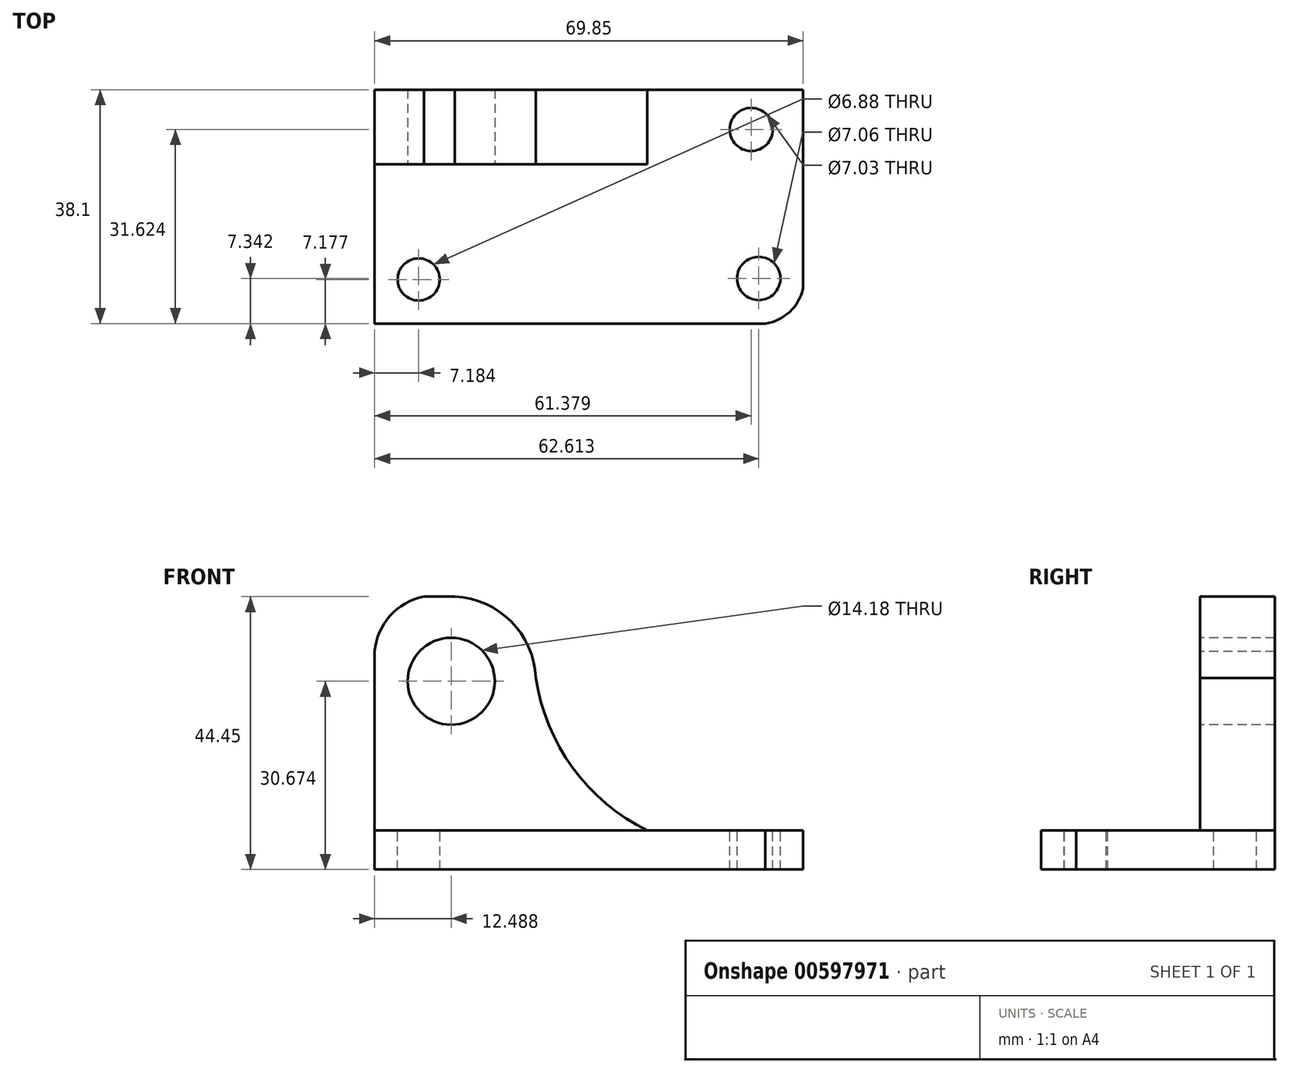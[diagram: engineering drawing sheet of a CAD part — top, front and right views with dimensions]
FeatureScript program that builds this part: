
annotation { "Feature Type Name" : "Feature", "Feature Type Description" : "" }
export const myFeature = defineFeature(function(context is Context, id is Id, definition is map)
    precondition{}
    {
        {
            var Q0;
            Q0=qCreatedBy(makeId("Front.planeOp"),FACE);
            var sketch = newSketch(context, id + "F0", { "sketchPlane" : qUnion([Q0])});
            skLineSegment(sketch, "E0", {"start": v(-44.83, 44.45) * mm, "end": v(-44.83, 0) * mm});
            skLineSegment(sketch, "E1", {"start": v(-44.83, 0) * mm, "end": v(25.02, 0) * mm});
            skLineSegment(sketch, "E2", {"start": v(25.02, 0) * mm, "end": v(25.02, 44.45) * mm});
            skLineSegment(sketch, "E3", {"start": v(25.02, 44.45) * mm, "end": v(-44.83, 44.45) * mm});
            skSolve(sketch);
        }
        {
            var Q0;
            Q0=makeQuery(id+"F0.imprint","IMPRINT",FACE,{"disambiguationData":[TD([[makeQuery(id+"F0.imprint","IMPRINT",EDGE,{"derivedFrom":sQuery(id+"F0.wireOp",EDGE,"E0")}),1.0]])]});
            extrude(context, id + "F1", {"entities" : qUnion([Q0]), "depth" : 38.1 * mm, "offsetDistance" : 25.4 * mm});
        }
        {
            var Q0;
            Q0=makeQuery(id+"F1.opExtrude","SWEPT_FACE",FACE,{"disambiguationData":[OSD([sQuery(id+"F0.wireOp",EDGE,"E3")])]});
            var sketch = newSketch(context, id + "F2", { "sketchPlane" : qUnion([Q0])});
            skArc(sketch, "E4", {"start": v(-44.83, -31.23) * mm, "mid": v(-42.48, -36.24) * mm, "end": v(-37.27, -38.1) * mm});
            skArc(sketch, "E5", {"start": v(18.85, -38.1) * mm, "mid": v(22.83, -36.2) * mm, "end": v(25.02, -32.38) * mm});
            skSolve(sketch);
        }
        {
            var Q0;
            {var subQ0=sQuery(id+"F2.wireOp",EDGE,"E4");var subQ1=sQuery(id+"F0.wireOp",EDGE,"E3");var subQ4=makeQuery(id+"F1.opExtrude","CAP_EDGE",EDGE,{"disambiguationData":[OSD([subQ1])],"isStart":false});var subQ5=makeQuery(id+"F2.imprint","INTERSECT",VERTEX,{"disambiguationData":[OD(1.0)],"derivedFrom":[subQ4,subQ0]});Q0=makeQuery(id+"F2.imprint","IMPRINT",FACE,{"disambiguationData":[TD([[makeQuery(id+"F2.imprint","IMPRINT",EDGE,{"disambiguationData":[TD([[subQ5,1.0]])],"derivedFrom":subQ0}),-1.0]])]});}
            var Q1;
            {var subQ0=sQuery(id+"F2.wireOp",EDGE,"E5");Q1=makeQuery(id+"F2.imprint","IMPRINT",FACE,{"disambiguationData":[TD([[makeQuery(id+"F2.imprint","IMPRINT",EDGE,{"derivedFrom":subQ0}),-1.0]])]});}
            extrude(context, id + "F3", {"entities" : qUnion([Q0, Q1]), "operationType" : NewBodyOperationType.REMOVE, "endBound" : BoundingType.THROUGH_ALL, "oppositeDirection" : true, "depth" : 25.4 * mm, "offsetDistance" : 25.4 * mm});
        }
        {
            var Q0;
            Q0=makeQuery(id+"F1.opExtrude","SWEPT_FACE",FACE,{"disambiguationData":[OSD([sQuery(id+"F0.wireOp",EDGE,"E3")])]});
            var sketch = newSketch(context, id + "F4", { "sketchPlane" : qUnion([Q0])});
            skLineSegment(sketch, "E6", {"start": v(-44.83, -12.18) * mm, "end": v(-0.38, -12.18) * mm});
            skLineSegment(sketch, "E7", {"start": v(-0.38, -12.18) * mm, "end": v(-0.38, 0) * mm});
            skSolve(sketch);
        }
        {
            var Q0;
            {var subQ2=sQuery(id+"F4.wireOp",EDGE,"E6");Q0=makeQuery(id+"F4.imprint","IMPRINT",FACE,{"disambiguationData":[TD([[makeQuery(id+"F4.imprint","IMPRINT",EDGE,{"derivedFrom":subQ2}),-1.0]])]});}
            extrude(context, id + "F5", {"entities" : qUnion([Q0]), "operationType" : NewBodyOperationType.REMOVE, "oppositeDirection" : true, "depth" : 31.75 * mm, "offsetDistance" : 25.4 * mm});
        }
        {
            var Q0;
            Q0=makeQuery(id+"F5.boolean.opBoolean","COPY",FACE,{"derivedFrom":makeQuery(id+"F5.opExtrude","CAP_FACE",FACE,{"disambiguationData":[OSD([sQuery(id+"F0.wireOp",EDGE,"E0"),sQuery(id+"F0.wireOp",EDGE,"E2"),sQuery(id+"F0.wireOp",EDGE,"E3"),sQuery(id+"F2.wireOp",EDGE,"E4"),sQuery(id+"F2.wireOp",EDGE,"E5"),sQuery(id+"F4.wireOp",EDGE,"E6"),sQuery(id+"F4.wireOp",EDGE,"E7")])],"isStart":false})});
            extrude(context, id + "F6", {"entities" : qUnion([Q0]), "operationType" : NewBodyOperationType.ADD, "depth" : 5.08 * mm, "offsetDistance" : 25.4 * mm});
        }
        {
            var Q0;
            Q0=makeQuery(id+"F6.opExtrude","CAP_FACE",FACE,{"disambiguationData":[OSD([sQuery(id+"F0.wireOp",EDGE,"E0"),sQuery(id+"F0.wireOp",EDGE,"E2"),sQuery(id+"F0.wireOp",EDGE,"E3"),sQuery(id+"F2.wireOp",EDGE,"E4"),sQuery(id+"F2.wireOp",EDGE,"E5"),sQuery(id+"F4.wireOp",EDGE,"E6"),sQuery(id+"F4.wireOp",EDGE,"E7")])],"isStart":false});
            extrude(context, id + "F7", {"entities" : qUnion([Q0]), "operationType" : NewBodyOperationType.REMOVE, "oppositeDirection" : true, "depth" : 6.35 * mm, "offsetDistance" : 25.4 * mm});
        }
        {
            var Q0;
            Q0=makeQuery(id+"F7.boolean.opBoolean","COPY",FACE,{"derivedFrom":makeQuery(id+"F7.opExtrude","CAP_FACE",FACE,{"disambiguationData":[OSD([sQuery(id+"F0.wireOp",EDGE,"E0"),sQuery(id+"F0.wireOp",EDGE,"E2"),sQuery(id+"F0.wireOp",EDGE,"E3"),sQuery(id+"F2.wireOp",EDGE,"E4"),sQuery(id+"F2.wireOp",EDGE,"E5"),sQuery(id+"F4.wireOp",EDGE,"E6"),sQuery(id+"F4.wireOp",EDGE,"E7")])],"isStart":false})});
            extrude(context, id + "F8", {"entities" : qUnion([Q0]), "operationType" : NewBodyOperationType.REMOVE, "oppositeDirection" : true, "depth" : 5.08 * mm, "offsetDistance" : 25.4 * mm});
        }
        {
            var Q0;
            {var subQ0=sQuery(id+"F4.wireOp",EDGE,"E6");Q0=makeQuery(id+"F8.boolean.opBoolean","MERGE",FACE,{"derivedFrom":[makeQuery(id+"F7.boolean.opBoolean","MERGE",FACE,{"derivedFrom":[makeQuery(id+"F5.boolean.opBoolean","COPY",FACE,{"derivedFrom":makeQuery(id+"F5.opExtrude","SWEPT_FACE",FACE,{"disambiguationData":[OSD([subQ0])]})}),makeQuery(id+"F7.opExtrude","SWEPT_FACE",FACE,{"disambiguationData":[OSD([subQ0])]})]}),makeQuery(id+"F8.opExtrude","SWEPT_FACE",FACE,{"disambiguationData":[OSD([subQ0])]})]});}
            var sketch = newSketch(context, id + "F9", { "sketchPlane" : qUnion([Q0])});
            skArc(sketch, "E8", {"start": v(-32.95, 44.45) * mm, "mid": v(-40.87, 42.63) * mm, "end": v(-44.83, 35.54) * mm});
            skArc(sketch, "E9", {"start": v(-18.56, 31.23) * mm, "mid": v(-23.01, 40.83) * mm, "end": v(-32.95, 44.45) * mm});
            skArc(sketch, "E10", {"start": v(-18.56, 31.23) * mm, "mid": v(-12.52, 16.56) * mm, "end": v(-0.38, 6.35) * mm});
            skSolve(sketch);
        }
        {
            var Q0;
            {var subQ0=sQuery(id+"F9.wireOp",EDGE,"E8");var subQ1=sQuery(id+"F4.wireOp",EDGE,"E6");var subQ6=makeQuery(id+"F5.boolean.opBoolean","COPY",EDGE,{"derivedFrom":makeQuery(id+"F5.opExtrude","CAP_EDGE",EDGE,{"disambiguationData":[OSD([subQ1])],"isStart":true})});var subQ7=makeQuery(id+"F9.imprint","INTERSECT",VERTEX,{"derivedFrom":[subQ6,subQ0]});Q0=makeQuery(id+"F9.imprint","IMPRINT",FACE,{"disambiguationData":[TD([[makeQuery(id+"F9.imprint","IMPRINT",EDGE,{"disambiguationData":[TD([[subQ7,-1.0]])],"derivedFrom":subQ0}),-1.0]])]});}
            var Q1;
            {var subQ0=sQuery(id+"F9.wireOp",EDGE,"E10");Q1=makeQuery(id+"F9.imprint","IMPRINT",FACE,{"disambiguationData":[TD([[makeQuery(id+"F9.imprint","IMPRINT",EDGE,{"derivedFrom":subQ0}),1.0]])]});}
            extrude(context, id + "F10", {"entities" : qUnion([Q0, Q1]), "operationType" : NewBodyOperationType.REMOVE, "endBound" : BoundingType.THROUGH_ALL, "oppositeDirection" : true, "depth" : 25.4 * mm, "offsetDistance" : 25.4 * mm});
        }
        {
            var Q0;
            {var subQ0=sQuery(id+"F4.wireOp",EDGE,"E6");Q0=makeQuery(id+"F8.boolean.opBoolean","MERGE",FACE,{"derivedFrom":[makeQuery(id+"F7.boolean.opBoolean","MERGE",FACE,{"derivedFrom":[makeQuery(id+"F5.boolean.opBoolean","COPY",FACE,{"derivedFrom":makeQuery(id+"F5.opExtrude","SWEPT_FACE",FACE,{"disambiguationData":[OSD([subQ0])]})}),makeQuery(id+"F7.opExtrude","SWEPT_FACE",FACE,{"disambiguationData":[OSD([subQ0])]})]}),makeQuery(id+"F8.opExtrude","SWEPT_FACE",FACE,{"disambiguationData":[OSD([subQ0])]})]});}
            var sketch = newSketch(context, id + "F11", { "sketchPlane" : qUnion([Q0])});
            skCircle(sketch, "E11", {"center": v(-32.34, 30.67) * mm, "radius": 7.1 * mm});
            skSolve(sketch);
        }
        {
            var Q0;
            Q0=makeQuery(id+"F11.imprint","IMPRINT",FACE,{"disambiguationData":[TD([[makeQuery(id+"F11.imprint","IMPRINT",EDGE,{"derivedFrom":sQuery(id+"F11.wireOp",EDGE,"E11")}),1.0]])]});
            extrude(context, id + "F12", {"entities" : qUnion([Q0]), "operationType" : NewBodyOperationType.ADD, "endBound" : BoundingType.THROUGH_ALL, "depth" : 25.4 * mm, "offsetDistance" : 25.4 * mm});
        }
        {
            var Q0;
            Q0=makeQuery(id+"F12.opExtrude","CAP_FACE",FACE,{"disambiguationData":[OSD([sQuery(id+"F11.wireOp",EDGE,"E11")])],"isStart":false});
            extrude(context, id + "F13", {"entities" : qUnion([Q0]), "operationType" : NewBodyOperationType.REMOVE, "endBound" : BoundingType.THROUGH_ALL, "oppositeDirection" : true, "depth" : 25.4 * mm, "offsetDistance" : 25.4 * mm});
        }
        {
            var Q0;
            Q0=makeQuery(id+"F8.boolean.opBoolean","COPY",FACE,{"derivedFrom":makeQuery(id+"F8.opExtrude","CAP_FACE",FACE,{"disambiguationData":[OSD([sQuery(id+"F0.wireOp",EDGE,"E0"),sQuery(id+"F0.wireOp",EDGE,"E2"),sQuery(id+"F0.wireOp",EDGE,"E3"),sQuery(id+"F2.wireOp",EDGE,"E4"),sQuery(id+"F2.wireOp",EDGE,"E5"),sQuery(id+"F4.wireOp",EDGE,"E6"),sQuery(id+"F4.wireOp",EDGE,"E7")])],"isStart":false})});
            var sketch = newSketch(context, id + "F14", { "sketchPlane" : qUnion([Q0])});
            skCircle(sketch, "E12", {"center": v(16.55, -6.48) * mm, "radius": 3.51 * mm});
            skCircle(sketch, "E13", {"center": v(17.78, -30.76) * mm, "radius": 3.53 * mm});
            skCircle(sketch, "E14", {"center": v(-37.65, -30.92) * mm, "radius": 3.44 * mm});
            skSolve(sketch);
        }
        {
            var Q0;
            Q0 = qSketchRegion(id + "F14", true);
            extrude(context, id + "F15", {"entities" : qUnion([Q0]), "operationType" : NewBodyOperationType.REMOVE, "endBound" : BoundingType.THROUGH_ALL, "oppositeDirection" : true, "depth" : 25.4 * mm, "offsetDistance" : 25.4 * mm});
        }
    });
